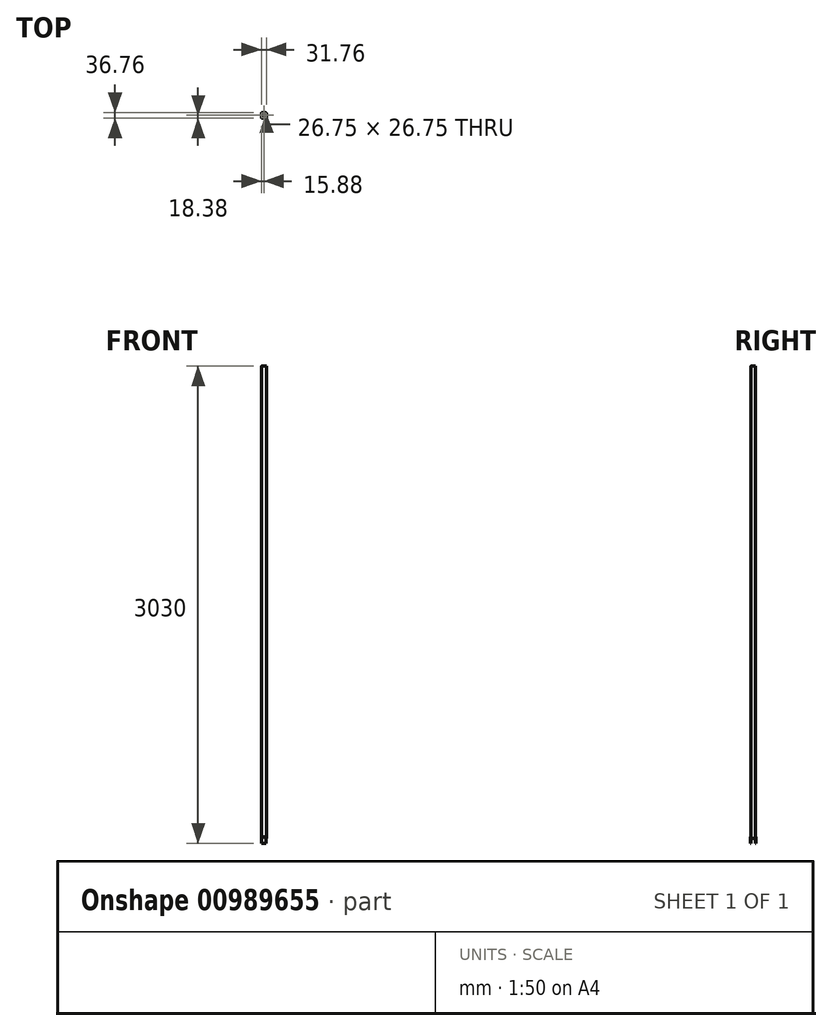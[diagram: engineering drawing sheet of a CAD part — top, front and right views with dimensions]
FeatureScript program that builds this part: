
annotation { "Feature Type Name" : "Feature", "Feature Type Description" : "" }
export const myFeature = defineFeature(function(context is Context, id is Id, definition is map)
    precondition{}
    {
        {
            var Q0;
            Q0=qCreatedBy(makeId("Top.planeOp"),FACE);
            var sketch = newSketch(context, id + "F0", { "sketchPlane" : qUnion([Q0])});
            skLineSegment(sketch, "E0.bottom", {"start": v(13.38, 15.88) * mm, "end": v(-13.38, 15.88) * mm});
            skLineSegment(sketch, "E0.top", {"start": v(13.37, -15.88) * mm, "end": v(-13.37, -15.88) * mm});
            skLineSegment(sketch, "E0.left", {"start": v(15.88, 13.38) * mm, "end": v(15.88, -13.37) * mm});
            skLineSegment(sketch, "E0.right", {"start": v(-15.88, 13.38) * mm, "end": v(-15.88, -13.37) * mm});
            skPoint(sketch, "E0.middle", {"position": v(0, 0) * mm});
            skPoint(sketch, "E1.visualSharp", {"position": v(-15.88, 15.88) * mm});
            skArc(sketch, "E1.filletArc", {"start": v(-13.38, 15.88) * mm, "mid": v(-15.14, 15.14) * mm, "end": v(-15.88, 13.38) * mm});
            skPoint(sketch, "E2.visualSharp", {"position": v(15.88, 15.88) * mm});
            skArc(sketch, "E2.filletArc", {"start": v(15.88, 13.38) * mm, "mid": v(15.14, 15.14) * mm, "end": v(13.38, 15.88) * mm});
            skPoint(sketch, "E3.visualSharp", {"position": v(15.88, -15.88) * mm});
            skArc(sketch, "E3.filletArc", {"start": v(13.37, -15.88) * mm, "mid": v(15.14, -15.14) * mm, "end": v(15.88, -13.37) * mm});
            skPoint(sketch, "E4.visualSharp", {"position": v(-15.88, -15.88) * mm});
            skArc(sketch, "E4.filletArc", {"start": v(-15.88, -13.37) * mm, "mid": v(-15.14, -15.14) * mm, "end": v(-13.37, -15.88) * mm});
            skLineSegment(sketch, "E5.0", {"start": v(13.38, 13.38) * mm, "end": v(13.38, 13.38) * mm});
            skLineSegment(sketch, "E5.1", {"start": v(13.38, 13.38) * mm, "end": v(13.38, -13.38) * mm});
            skLineSegment(sketch, "E5.2", {"start": v(13.38, 13.38) * mm, "end": v(-13.37, 13.38) * mm});
            skLineSegment(sketch, "E5.3", {"start": v(13.37, -13.37) * mm, "end": v(13.37, -13.37) * mm});
            skLineSegment(sketch, "E5.4", {"start": v(-13.37, 13.37) * mm, "end": v(-13.37, 13.37) * mm});
            skLineSegment(sketch, "E5.5", {"start": v(-13.37, 13.38) * mm, "end": v(-13.37, -13.38) * mm});
            skLineSegment(sketch, "E5.6", {"start": v(-13.37, -13.37) * mm, "end": v(-13.37, -13.37) * mm});
            skLineSegment(sketch, "E5.7", {"start": v(13.38, -13.38) * mm, "end": v(-13.37, -13.38) * mm});
            skSolve(sketch);
        }
        {
            var Q0;
            Q0=makeQuery(id+"F0.imprint","IMPRINT",FACE,{"disambiguationData":[TD([[makeQuery(id+"F0.imprint","IMPRINT",EDGE,{"derivedFrom":sQuery(id+"F0.wireOp",EDGE,"E0.bottom")}),1.0]])]});
            extrude(context, id + "F1", {"entities" : qUnion([Q0]), "depth" : 3000 * mm, "offsetDistance" : 25 * mm});
        }
        {
            var Q0;
            Q0=makeQuery(id+"F1.opExtrude","SWEPT_FACE",FACE,{"disambiguationData":[OSD([sQuery(id+"F0.wireOp",EDGE,"E0.top")])]});
            var sketch = newSketch(context, id + "F2", { "sketchPlane" : qUnion([Q0])});
            skLineSegment(sketch, "E6.bottom", {"start": v(-13.37, 10) * mm, "end": v(13.37, 10) * mm});
            skLineSegment(sketch, "E6.top", {"start": v(-13.37, -30) * mm, "end": v(13.37, -30) * mm});
            skLineSegment(sketch, "E6.left", {"start": v(-13.37, 10) * mm, "end": v(-13.37, -30) * mm});
            skLineSegment(sketch, "E6.right", {"start": v(13.37, 10) * mm, "end": v(13.37, -30) * mm});
            skSolve(sketch);
        }
        {
            var Q0;
            Q0=qSketchRegion(id+"F2",true);
            extrude(context, id + "F3", {"entities" : qUnion([Q0]), "depth" : 2.5 * mm, "offsetDistance" : 25 * mm});
        }
        {
            var Q0;
            Q0=makeQuery(id+"F3.opExtrude","SWEPT_BODY",BODY,{"disambiguationData":[OSD([sQuery(id+"F2.wireOp",EDGE,"L9w4inV8-05nj-Ykvd-Gynh-aTQAFaXWY75o.bottom"),sQuery(id+"F2.wireOp",EDGE,"L9w4inV8-05nj-Ykvd-Gynh-aTQAFaXWY75o.top"),sQuery(id+"F2.wireOp",EDGE,"L9w4inV8-05nj-Ykvd-Gynh-aTQAFaXWY75o.left"),sQuery(id+"F2.wireOp",EDGE,"L9w4inV8-05nj-Ykvd-Gynh-aTQAFaXWY75o.right")])]});
            var Q1;
            Q1=makeQuery(id+"F3.opExtrude","SWEPT_BODY",BODY,{"disambiguationData":[OSD([sQuery(id+"F2.wireOp",EDGE,"E6.bottom"),sQuery(id+"F2.wireOp",EDGE,"E6.top"),sQuery(id+"F2.wireOp",EDGE,"E6.left"),sQuery(id+"F2.wireOp",EDGE,"E6.right")])]});
            var Q2;
            Q2=qCreatedBy(makeId("Front.planeOp"),FACE);
            mirror(context, id + "F4", {"operationType" : NewBodyOperationType.ADD, "entities" : qUnion([Q0, Q1]), "mirrorPlane" : qUnion([Q2])});
        }
    });
